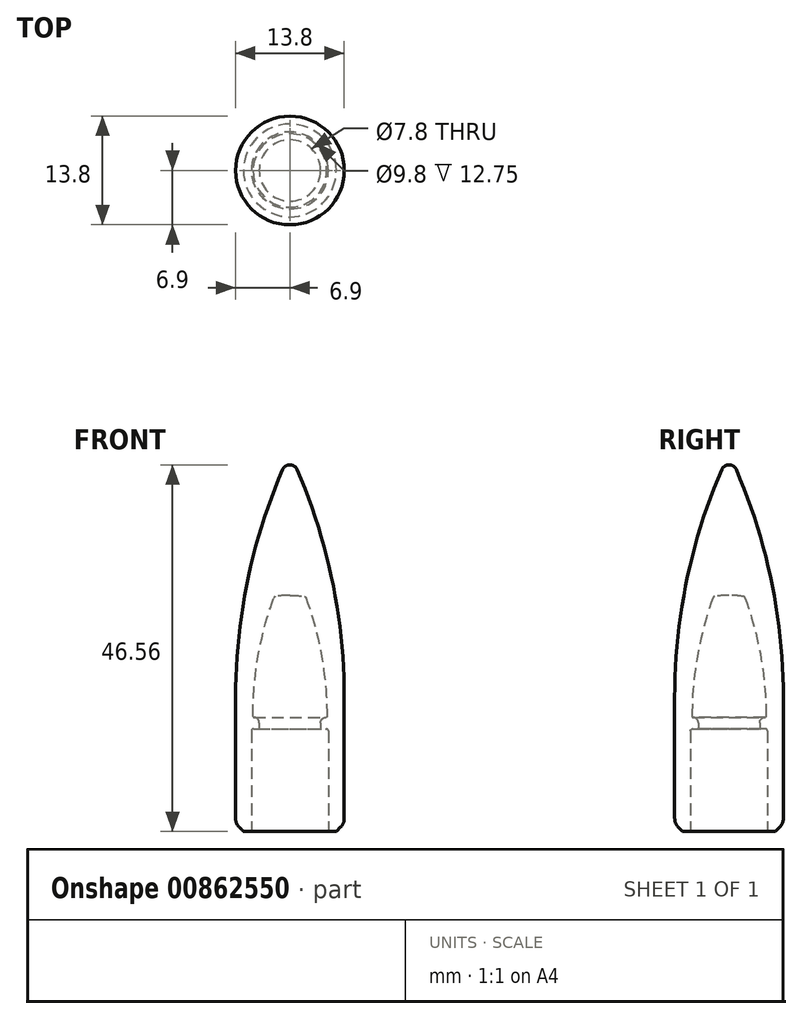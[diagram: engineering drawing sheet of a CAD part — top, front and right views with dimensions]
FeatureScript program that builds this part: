
annotation { "Feature Type Name" : "Feature", "Feature Type Description" : "" }
export const myFeature = defineFeature(function(context is Context, id is Id, definition is map)
    precondition{}
    {
        {
            var Q0;
            Q0=qCreatedBy(makeId("Front.planeOp"),FACE);
            var sketch = newSketch(context, id + "F0", { "sketchPlane" : qUnion([Q0])});
            skLineSegment(sketch, "E0", {"start": v(0, 4.32) * mm, "end": v(0, -4.92) * mm, "construction": true});
            skArc(sketch, "E1", {"start": v(6.9, 4) * mm, "mid": v(5.39, 18.79) * mm, "end": v(0.92, 32.96) * mm});
            skLineSegment(sketch, "E2", {"start": v(6.9, 4) * mm, "end": v(6.9, -11.38) * mm});
            skLineSegment(sketch, "E3", {"start": v(5.9, -13) * mm, "end": v(4.9, -13) * mm});
            skLineSegment(sketch, "E4", {"start": v(4.9, -13) * mm, "end": v(4.9, -0.25) * mm});
            skLineSegment(sketch, "E5", {"start": v(4.65, 0) * mm, "end": v(4, 0) * mm});
            skLineSegment(sketch, "E6", {"start": v(3.9, 0.1) * mm, "end": v(3.9, 0.8) * mm});
            skLineSegment(sketch, "E7", {"start": v(4.6, 1.5) * mm, "end": v(4.6, 1.5) * mm});
            skArc(sketch, "E8", {"start": v(0.92, 32.96) * mm, "mid": v(0.55, 33.4) * mm, "end": v(0, 33.56) * mm});
            skPoint(sketch, "E9.orphan", {"position": v(0, 35) * mm});
            skLineSegment(sketch, "E10", {"start": v(0, 17) * mm, "end": v(0, 33.56) * mm});
            skLineSegment(sketch, "E11", {"start": v(5.9, -13) * mm, "end": v(6.46, -12.44) * mm});
            skPoint(sketch, "E12.orphan", {"position": v(6.9, -13) * mm});
            skPoint(sketch, "E13.visualSharp", {"position": v(4.9, 0) * mm});
            skArc(sketch, "E13.filletArc", {"start": v(4.9, -0.25) * mm, "mid": v(4.83, -0.07) * mm, "end": v(4.65, 0) * mm});
            skPoint(sketch, "E14.visualSharp", {"position": v(4.9, 1.5) * mm});
            skArc(sketch, "E14.filletArc", {"start": v(4.6, 1.5) * mm, "mid": v(4.67, 1.53) * mm, "end": v(4.7, 1.6) * mm});
            skPoint(sketch, "E15.visualSharp", {"position": v(3.9, 1.5) * mm});
            skArc(sketch, "E15.filletArc", {"start": v(4.6, 1.5) * mm, "mid": v(4.1, 1.3) * mm, "end": v(3.9, 0.8) * mm});
            skPoint(sketch, "E16.visualSharp", {"position": v(3.9, 0) * mm});
            skArc(sketch, "E16.filletArc", {"start": v(3.9, 0.1) * mm, "mid": v(3.93, 0.03) * mm, "end": v(4, 0) * mm});
            skArc(sketch, "E17", {"start": v(4.7, 1.6) * mm, "mid": v(4.02, 9.25) * mm, "end": v(2.05, 16.66) * mm});
            skArc(sketch, "E18.trimOffspring", {"start": v(1.86, 16.83) * mm, "mid": v(0.93, 16.96) * mm, "end": v(0, 17) * mm});
            skPoint(sketch, "E19.visualSharp", {"position": v(2, 16.8) * mm});
            skArc(sketch, "E19.filletArc", {"start": v(2.05, 16.66) * mm, "mid": v(1.98, 16.77) * mm, "end": v(1.86, 16.83) * mm});
            skPoint(sketch, "E20.visualSharp", {"position": v(6.9, -12) * mm});
            skArc(sketch, "E20.filletArc", {"start": v(6.46, -12.44) * mm, "mid": v(6.79, -11.95) * mm, "end": v(6.9, -11.38) * mm});
            skSolve(sketch);
        }
        {
            var Q0;
            Q0=makeQuery(id+"F0.imprint","IMPRINT",FACE,{"disambiguationData":[TD([[makeQuery(id+"F0.imprint","IMPRINT",EDGE,{"derivedFrom":sQuery(id+"F0.wireOp",EDGE,"E1")}),1.0]])]});
            var Q1;
            Q1=sQuery(id+"F0.wireOp",EDGE,"E10");
            revolve(context, id + "F1", {"surfaceOperationType" : NewSurfaceOperationType.NEW, "entities" : qUnion([Q0]), "axis" : qUnion([Q1]), "revolveType" : RevolveType.FULL});
        }
    });
